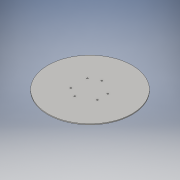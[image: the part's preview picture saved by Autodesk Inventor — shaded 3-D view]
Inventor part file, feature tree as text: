
AUTODESK INVENTOR PART (.ipt)
format: ipt  version: 2016 (Build 200138000, 138)  size: 102,400 bytes
history: native  units: in
note: dims shown in document units (in); Inventor stores cm internally (conversion verified against a paired STEP export)
features: sketch x2, extrude x1, hole x1
ambient origin geometry x8: Origin, YZ Plane, XZ Plane, XY Plane, X Axis, Y Axis, Z Axis, Center Point
bodies: Solid1 (feature_tree)
feature tree (4):
  extrude  "Extrusion1"  Depth=0.125in TaperAngle=0.0deg
  hole  "Hole1"  [1 undecoded]
  sketch  "Sketch1"  dims[d0=12.0in d1=0.125in d2=0.0in]
  sketch  "Sketch2"  dims[d4=1.8in d5=0.75in d6=0.75in d7=1.8in d8=1.1811in d10=360.0deg d12=0.1969in d13=0.75in d14=0.375in d15=0.25in d16=0.5635in d17=1.0in d18=0.8108in]
note: 1 required parameter value undecoded (feature->parameter linkage not recoverable at this tier; creation-order binding heuristic only, values carry confidence <= 0.55)
